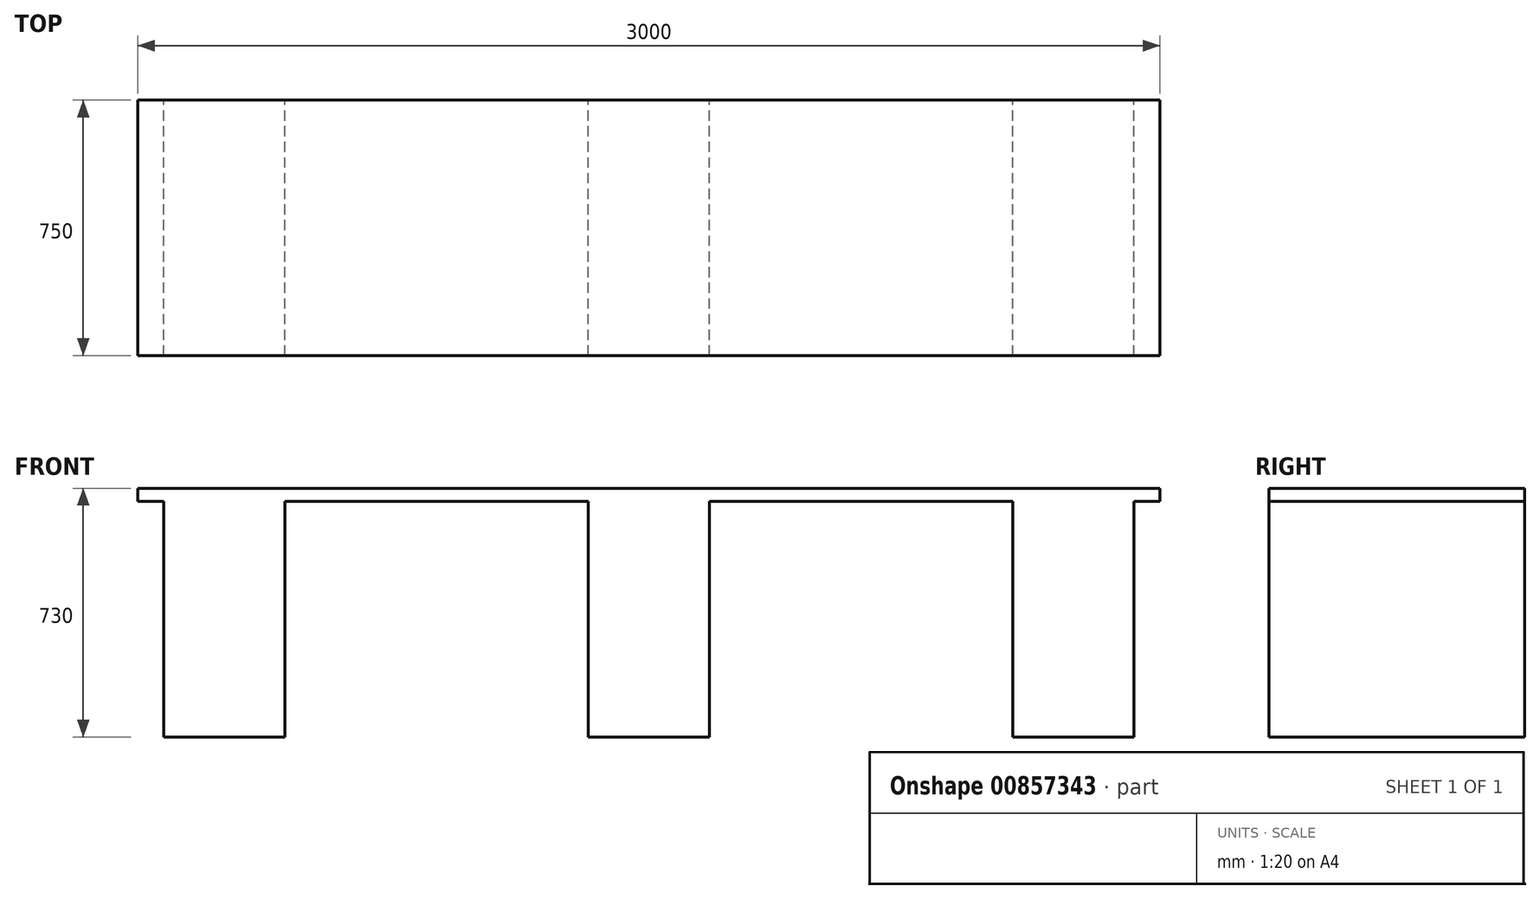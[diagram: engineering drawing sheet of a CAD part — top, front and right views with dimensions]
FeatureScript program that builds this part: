
annotation { "Feature Type Name" : "Feature", "Feature Type Description" : "" }
export const myFeature = defineFeature(function(context is Context, id is Id, definition is map)
    precondition{}
    {
        {
            var Q0;
            Q0=qCreatedBy(makeId("Front.planeOp"),FACE);
            var sketch = newSketch(context, id + "F0", { "sketchPlane" : qUnion([Q0])});
            skLineSegment(sketch, "E0.bottom", {"start": v(76.2, 0) * mm, "end": v(431.8, 0) * mm});
            skLineSegment(sketch, "E0.top", {"start": v(0, 730) * mm, "end": v(3000, 730) * mm});
            skLineSegment(sketch, "E0.left", {"start": v(0, 691.9) * mm, "end": v(0, 730) * mm});
            skLineSegment(sketch, "E0.right", {"start": v(3000, 691.9) * mm, "end": v(3000, 730) * mm});
            skLineSegment(sketch, "E1", {"start": v(0, 691.9) * mm, "end": v(76.2, 691.9) * mm});
            skLineSegment(sketch, "E2", {"start": v(76.2, 691.9) * mm, "end": v(76.2, 0) * mm});
            skLineSegment(sketch, "E3", {"start": v(3000, 691.9) * mm, "end": v(2923.8, 691.9) * mm});
            skLineSegment(sketch, "E4", {"start": v(2923.8, 691.9) * mm, "end": v(2923.8, 0) * mm});
            skLineSegment(sketch, "E5", {"start": v(431.8, 0) * mm, "end": v(431.8, 691.9) * mm});
            skLineSegment(sketch, "E6", {"start": v(431.8, 691.9) * mm, "end": v(1322.2, 691.9) * mm});
            skLineSegment(sketch, "E7", {"start": v(1322.2, 691.9) * mm, "end": v(1322.2, 0) * mm});
            skPoint(sketch, "E8", {"position": v(1500, 0) * mm});
            skLineSegment(sketch, "E9", {"start": v(2568.2, 0) * mm, "end": v(2568.2, 691.9) * mm});
            skLineSegment(sketch, "E10", {"start": v(2568.2, 691.9) * mm, "end": v(1677.8, 691.9) * mm});
            skLineSegment(sketch, "E11", {"start": v(1677.8, 691.9) * mm, "end": v(1677.8, 0) * mm});
            skLineSegment(sketch, "E12.trimOffspring", {"start": v(1322.2, 0) * mm, "end": v(1677.8, 0) * mm});
            skLineSegment(sketch, "E13.trimOffspring", {"start": v(2568.2, 0) * mm, "end": v(2923.8, 0) * mm});
            skSolve(sketch);
        }
        {
            var Q0;
            Q0 = qSketchRegion(id + "F0", true);
            extrude(context, id + "F1", {"entities" : qUnion([Q0]), "depth" : 750 * mm, "offsetDistance" : 25.4 * mm});
        }
    });
